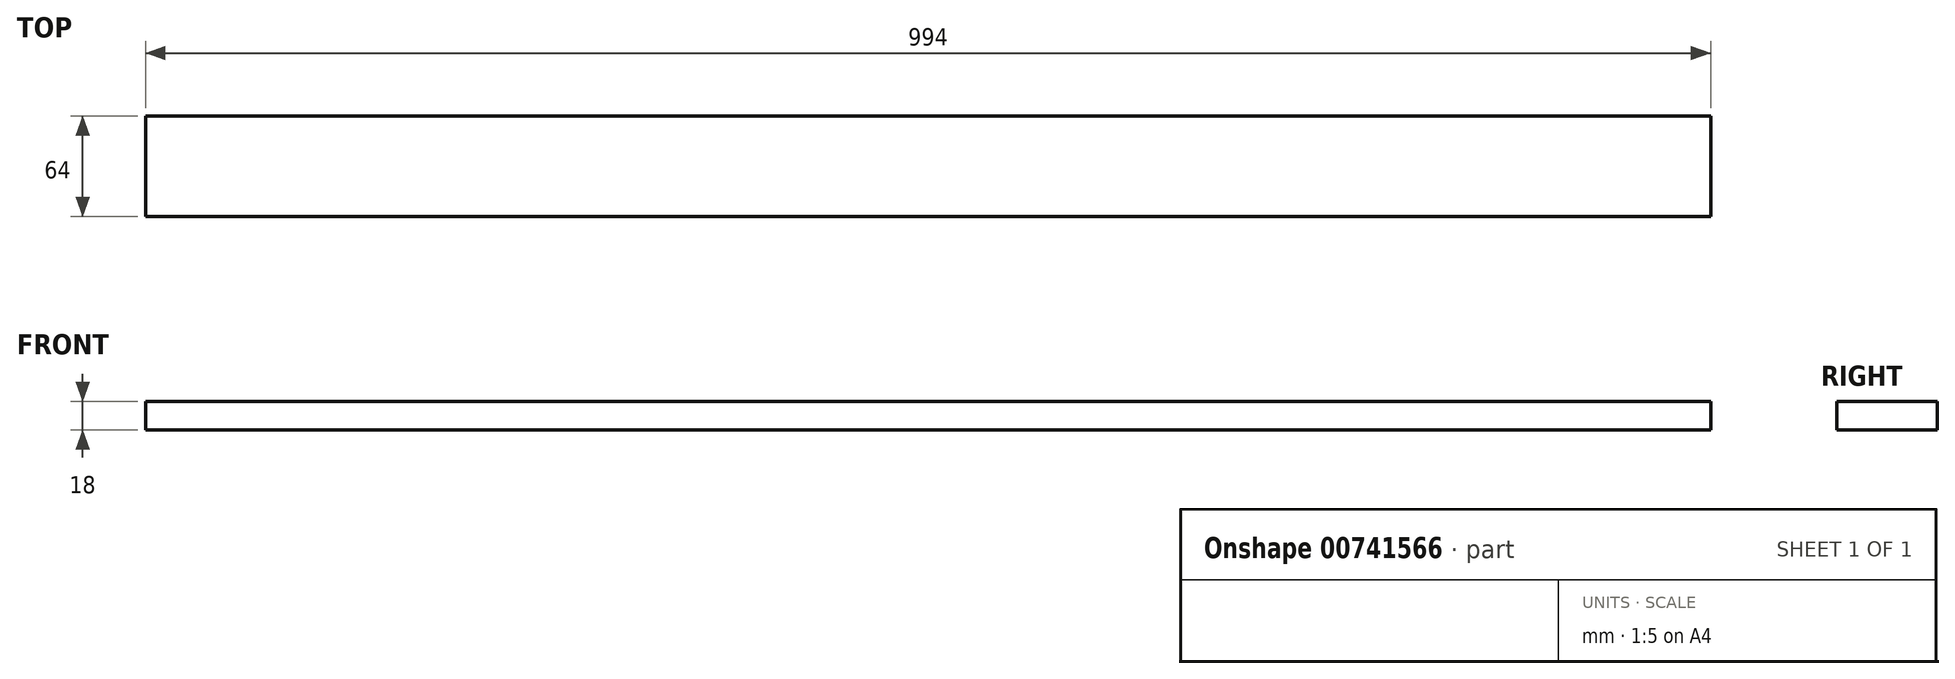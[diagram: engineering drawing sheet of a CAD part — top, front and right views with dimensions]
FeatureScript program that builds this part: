
annotation { "Feature Type Name" : "Feature", "Feature Type Description" : "" }
export const myFeature = defineFeature(function(context is Context, id is Id, definition is map)
    precondition{}
    {
        {
            var Q0;
            Q0=qCreatedBy(makeId("Top.planeOp"),FACE);
            var sketch = newSketch(context, id + "F0", { "sketchPlane" : qUnion([Q0])});
            skLineSegment(sketch, "E0.bottom", {"start": v(-497, -32) * mm, "end": v(497, -32) * mm});
            skLineSegment(sketch, "E0.top", {"start": v(-497, 32) * mm, "end": v(497, 32) * mm});
            skLineSegment(sketch, "E0.left", {"start": v(-497, -32) * mm, "end": v(-497, 32) * mm});
            skLineSegment(sketch, "E0.right", {"start": v(497, -32) * mm, "end": v(497, 32) * mm});
            skPoint(sketch, "E0.middle", {"position": v(0, 0) * mm});
            skSolve(sketch);
        }
        {
            var Q0;
            Q0=qSketchRegion(id+"F0",true);
            extrude(context, id + "F1", {"entities" : qUnion([Q0]), "depth" : 18 * mm, "offsetDistance" : 25 * mm});
        }
    });
